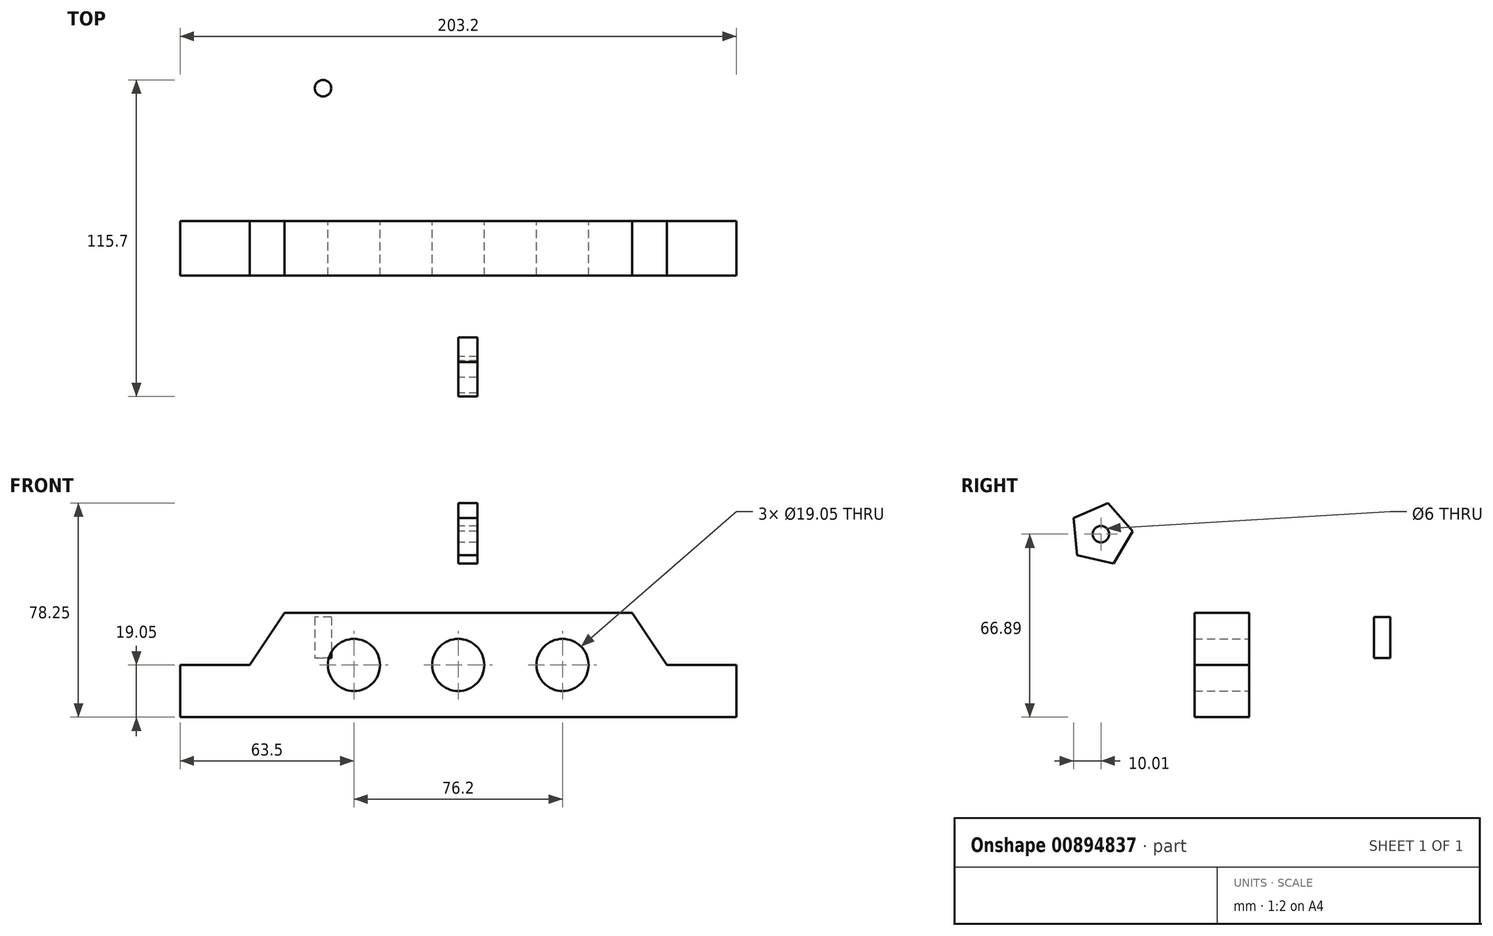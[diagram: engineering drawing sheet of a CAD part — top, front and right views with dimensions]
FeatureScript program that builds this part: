
annotation { "Feature Type Name" : "Feature", "Feature Type Description" : "" }
export const myFeature = defineFeature(function(context is Context, id is Id, definition is map)
    precondition{}
    {
        {
            var Q0;
            Q0=qCreatedBy(makeId("Front.planeOp"),FACE);
            var sketch = newSketch(context, id + "F0", { "sketchPlane" : qUnion([Q0])});
            skLineSegment(sketch, "E0.bottom", {"start": v(-63.5, 16.5) * mm, "end": v(63.5, 16.5) * mm});
            skLineSegment(sketch, "E0.top", {"start": v(-101.6, -21.59) * mm, "end": v(101.6, -21.59) * mm});
            skLineSegment(sketch, "E0.left", {"start": v(-101.6, -2.54) * mm, "end": v(-101.6, -21.59) * mm});
            skLineSegment(sketch, "E0.right", {"start": v(101.6, -2.54) * mm, "end": v(101.6, -21.59) * mm});
            skLineSegment(sketch, "E1", {"start": v(-101.6, -2.54) * mm, "end": v(-76.2, -2.54) * mm});
            skLineSegment(sketch, "E2", {"start": v(-76.2, -2.54) * mm, "end": v(-63.5, 16.51) * mm});
            skCircle(sketch, "E3", {"center": v(-38.1, -2.54) * mm, "radius": 9.53 * mm});
            skCircle(sketch, "E4", {"center": v(0, -2.54) * mm, "radius": 9.53 * mm});
            skPoint(sketch, "E5.orphan", {"position": v(-101.6, 16.5) * mm});
            skLineSegment(sketch, "E6.MirrorCS", {"start": v(76.2, -2.54) * mm, "end": v(63.5, 16.51) * mm});
            skLineSegment(sketch, "E7.MirrorCS", {"start": v(101.6, -2.54) * mm, "end": v(76.2, -2.54) * mm});
            skPoint(sketch, "E8.orphan", {"position": v(101.6, 16.5) * mm});
            skCircle(sketch, "E9.MirrorC", {"center": v(38.1, -2.54) * mm, "radius": 9.53 * mm});
            skPoint(sketch, "E10.orphan", {"position": v(0, 16.5) * mm});
            skPoint(sketch, "E11.orphan", {"position": v(0, -21.59) * mm});
            skSolve(sketch);
        }
        {
            var Q0;
            Q0=makeQuery(id+"F0.imprint","IMPRINT",FACE,{"disambiguationData":[TD([[makeQuery(id+"F0.imprint","IMPRINT",EDGE,{"derivedFrom":sQuery(id+"F0.wireOp",EDGE,"E0.bottom")}),-1.0]])]});
            extrude(context, id + "F1", {"entities" : qUnion([Q0]), "depth" : 20 * mm, "offsetDistance" : 25 * mm});
        }
        {
            var Q0;
            Q0=qCreatedBy(makeId("Top.planeOp"),FACE);
            var sketch = newSketch(context, id + "F2", { "sketchPlane" : qUnion([Q0])});
            skCircle(sketch, "E12", {"center": v(-49.39, 48.54) * mm, "radius": 3 * mm});
            skSolve(sketch);
        }
        {
            var Q0;
            Q0=makeQuery(id+"F2.imprint","IMPRINT",FACE,{"disambiguationData":[TD([[makeQuery(id+"F2.imprint","IMPRINT",EDGE,{"derivedFrom":sQuery(id+"F2.wireOp",EDGE,"E12")}),1.0]])]});
            extrude(context, id + "F3", {"entities" : qUnion([Q0]), "depth" : 15 * mm, "offsetDistance" : 25 * mm});
        }
        {
            var Q0;
            Q0=qCreatedBy(makeId("Right.planeOp"),FACE);
            var sketch = newSketch(context, id + "F4", { "sketchPlane" : qUnion([Q0])});
            skCircle(sketch, "E13.cCircle", {"center": v(-54.15, 45.3) * mm, "radius": 9.42 * mm, "construction": true});
            skLineSegment(sketch, "E13.0", {"start": v(-42.56, 46.39) * mm, "end": v(-49.54, 34.62) * mm});
            skLineSegment(sketch, "E13.1", {"start": v(-49.54, 34.62) * mm, "end": v(-62.89, 37.61) * mm});
            skLineSegment(sketch, "E13.2", {"start": v(-62.89, 37.61) * mm, "end": v(-64.16, 51.23) * mm});
            skLineSegment(sketch, "E13.3", {"start": v(-64.16, 51.23) * mm, "end": v(-51.6, 56.66) * mm});
            skLineSegment(sketch, "E13.4", {"start": v(-51.6, 56.66) * mm, "end": v(-42.56, 46.39) * mm});
            skPoint(sketch, "E13.0.midPoint", {"position": v(-46.05, 40.5) * mm});
            skSolve(sketch);
        }
        {
            var Q0;
            Q0=qSketchRegion(id+"F4",true);
            extrude(context, id + "F5", {"entities" : qUnion([Q0]), "depth" : 7 * mm, "offsetDistance" : 25 * mm});
        }
        {
            var Q0;
            Q0=makeQuery(id+"F5.opExtrude","CAP_FACE",FACE,{"disambiguationData":[OSD([sQuery(id+"F4.wireOp",EDGE,"E13.0"),sQuery(id+"F4.wireOp",EDGE,"E13.1"),sQuery(id+"F4.wireOp",EDGE,"E13.2"),sQuery(id+"F4.wireOp",EDGE,"E13.3"),sQuery(id+"F4.wireOp",EDGE,"E13.4")])],"isStart":true});
            var sketch = newSketch(context, id + "F6", { "sketchPlane" : qUnion([Q0])});
            skCircle(sketch, "E14", {"center": v(54.15, 45.3) * mm, "radius": 11.64 * mm});
            skSolve(sketch);
        }
        {
            var Q0;
            Q0=sQuery(id+"F6.wireOp",VERTEX,"E14.center");
            var Q1;
            Q1=makeQuery(id+"F5.opExtrude","SWEPT_BODY",BODY,{"disambiguationData":[OSD([sQuery(id+"F4.wireOp",EDGE,"E13.0"),sQuery(id+"F4.wireOp",EDGE,"E13.1"),sQuery(id+"F4.wireOp",EDGE,"E13.2"),sQuery(id+"F4.wireOp",EDGE,"E13.3"),sQuery(id+"F4.wireOp",EDGE,"E13.4")])]});
            hole(context, id + "F7", {"style" : HoleStyle.SIMPLE, "endStyle" : HoleEndStyle.THROUGH, "holeDiameter" : 6 * mm, "majorDiameter" : 5 * mm, "isTappedThrough" : true, "tappedDepth" : 12 * mm, "tapClearance" : 3, "locations" : qUnion([Q0]), "scope" : qUnion([Q1])});
        }
    });
